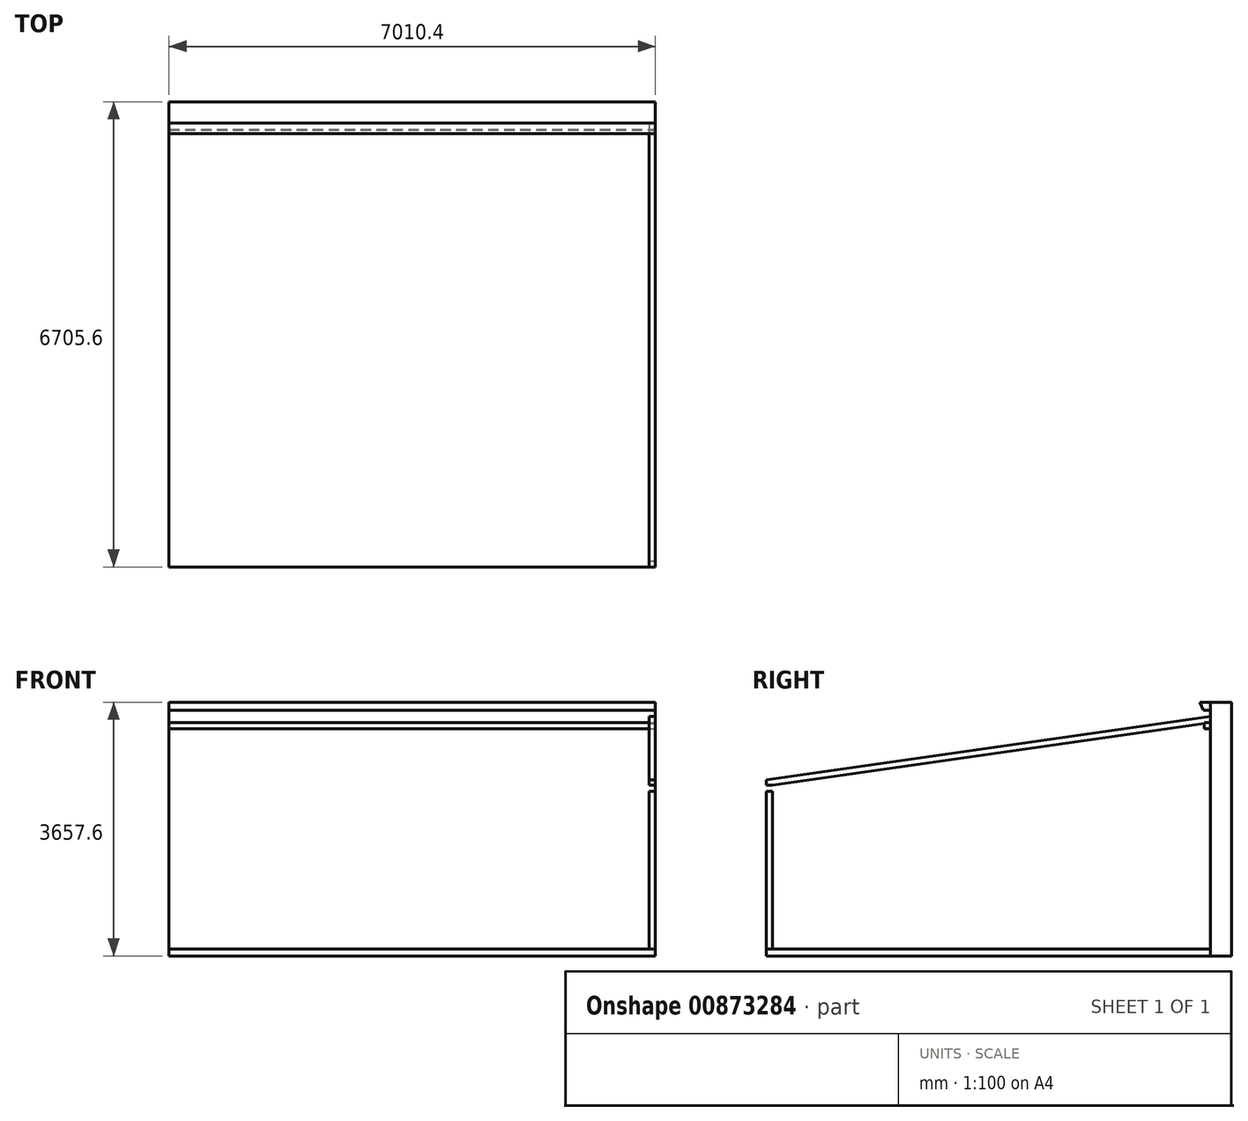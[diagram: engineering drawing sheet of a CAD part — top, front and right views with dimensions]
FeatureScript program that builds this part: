
annotation { "Feature Type Name" : "Feature", "Feature Type Description" : "" }
export const myFeature = defineFeature(function(context is Context, id is Id, definition is map)
    precondition{}
    {
        {
            var Q0;
            Q0=qCreatedBy(makeId("Front.planeOp"),FACE);
            var sketch = newSketch(context, id + "F0", { "sketchPlane" : qUnion([Q0])});
            skLineSegment(sketch, "E0", {"start": v(0, 0) * mm, "end": v(3505.2, 0) * mm});
            skLineSegment(sketch, "E1", {"start": v(0, 0) * mm, "end": v(-3505.2, 0) * mm});
            skLineSegment(sketch, "E2.bottom", {"start": v(-3505.2, 0) * mm, "end": v(3505.2, 0) * mm});
            skLineSegment(sketch, "E2.top", {"start": v(-3505.2, 3657.6) * mm, "end": v(3505.2, 3657.6) * mm});
            skLineSegment(sketch, "E2.left", {"start": v(-3505.2, 0) * mm, "end": v(-3505.2, 3657.6) * mm});
            skLineSegment(sketch, "E2.right", {"start": v(3505.2, 0) * mm, "end": v(3505.2, 3657.6) * mm});
            skSolve(sketch);
        }
        {
            var Q0;
            Q0=sQuery(id+"F0.wireOp",EDGE,"E1");
            var Q1;
            Q1=sQuery(id+"F0.wireOp",EDGE,"E0");
            extrude(context, id + "F1", {"bodyType" : ToolBodyType.SURFACE, "surfaceEntities" : qUnion([Q0, Q1]), "depth" : 6400.8 * mm, "offsetDistance" : 25 * mm});
        }
        {
            var Q0;
            Q0 = qSketchRegion(id + "F0", true);
            extrude(context, id + "F2", {"entities" : qUnion([Q0]), "oppositeDirection" : true, "depth" : 304.8 * mm, "offsetDistance" : 25 * mm});
        }
        {
            var Q0;
            Q0=makeQuery(id+"F2.opExtrude","SWEPT_FACE",FACE,{"disambiguationData":[OSD([sQuery(id+"F0.wireOp",EDGE,"E2.right")])]});
            var sketch = newSketch(context, id + "F3", { "sketchPlane" : qUnion([Q0])});
            skLineSegment(sketch, "E3", {"start": v(0, 3657.6) * mm, "end": v(0, 3543.3) * mm});
            skLineSegment(sketch, "E4", {"start": v(0, 3543.3) * mm, "end": v(-101.6, 3543.3) * mm});
            skLineSegment(sketch, "E5", {"start": v(-101.6, 3543.3) * mm, "end": v(-152.4, 3657.6) * mm});
            skLineSegment(sketch, "E6", {"start": v(-152.4, 3657.6) * mm, "end": v(0, 3657.6) * mm});
            skSolve(sketch);
        }
        {
            var Q0;
            Q0=makeQuery(id+"F3.imprint","IMPRINT",FACE,{"disambiguationData":[TD([[makeQuery(id+"F3.imprint","IMPRINT",EDGE,{"derivedFrom":sQuery(id+"F3.wireOp",EDGE,"E3")}),1.0]])]});
            extrude(context, id + "F4", {"entities" : qUnion([Q0]), "oppositeDirection" : true, "depth" : 7010.4 * mm, "offsetDistance" : 25 * mm});
        }
        {
            var Q0;
            Q0=makeQuery(id+"F1.opExtrude","SWEPT_FACE",FACE,{"disambiguationData":[OSD([sQuery(id+"F0.wireOp",EDGE,"E0"),sQuery(id+"F0.wireOp",EDGE,"E1")])]});
            extrude(context, id + "F5", {"entities" : qUnion([Q0]), "depth" : 101.6 * mm, "offsetDistance" : 25 * mm});
        }
        {
            var Q0;
            Q0=makeQuery(id+"F2.opExtrude","SWEPT_FACE",FACE,{"disambiguationData":[OSD([sQuery(id+"F0.wireOp",EDGE,"E2.right")])]});
            var sketch = newSketch(context, id + "F6", { "sketchPlane" : qUnion([Q0])});
            skLineSegment(sketch, "E7", {"start": v(0, 0) * mm, "end": v(0, 101.6) * mm});
            skLineSegment(sketch, "E8", {"start": v(0, 101.6) * mm, "end": v(0, 3454.4) * mm});
            skLineSegment(sketch, "E9", {"start": v(0, 3454.4) * mm, "end": v(-6400.8, 2540) * mm});
            skLineSegment(sketch, "E10", {"start": v(0, 101.6) * mm, "end": v(-6400.8, 101.6) * mm});
            skLineSegment(sketch, "E11", {"start": v(-6400.8, 101.6) * mm, "end": v(-6400.8, 2540) * mm});
            skLineSegment(sketch, "E12", {"start": v(-6400.8, 2450.2) * mm, "end": v(0, 3364.6) * mm});
            skLineSegment(sketch, "E13", {"start": v(-6311.9, 2462.9) * mm, "end": v(-6311.9, 101.6) * mm});
            skLineSegment(sketch, "E14.bottom", {"start": v(0, 3364.6) * mm, "end": v(-88.9, 3364.6) * mm});
            skLineSegment(sketch, "E14.top", {"start": v(0, 3275.7) * mm, "end": v(-88.9, 3275.7) * mm});
            skLineSegment(sketch, "E14.left", {"start": v(0, 3364.6) * mm, "end": v(0, 3275.7) * mm});
            skLineSegment(sketch, "E14.right", {"start": v(-88.9, 3364.6) * mm, "end": v(-88.9, 3275.7) * mm});
            skSolve(sketch);
        }
        {
            var Q0;
            {var subQ3=sQuery(id+"F6.wireOp",EDGE,"E13");Q0=makeQuery(id+"F6.imprint","IMPRINT",FACE,{"disambiguationData":[TD([[makeQuery(id+"F6.imprint","IMPRINT",EDGE,{"derivedFrom":subQ3}),-1.0]])]});}
            extrude(context, id + "F7", {"entities" : qUnion([Q0]), "oppositeDirection" : true, "depth" : 88.9 * mm, "offsetDistance" : 25 * mm});
        }
        {
            var Q0;
            {var subQ4=sQuery(id+"F6.wireOp",EDGE,"E9");Q0=makeQuery(id+"F6.imprint","IMPRINT",FACE,{"disambiguationData":[TD([[makeQuery(id+"F6.imprint","IMPRINT",EDGE,{"derivedFrom":subQ4}),1.0]])]});}
            extrude(context, id + "F8", {"entities" : qUnion([Q0]), "oppositeDirection" : true, "depth" : 88.9 * mm, "offsetDistance" : 25 * mm});
        }
        {
            var Q0;
            {var subQ4=sQuery(id+"F6.wireOp",EDGE,"E14.top");Q0=makeQuery(id+"F6.imprint","IMPRINT",FACE,{"disambiguationData":[TD([[makeQuery(id+"F6.imprint","IMPRINT",EDGE,{"derivedFrom":subQ4}),-1.0]])]});}
            var Q1;
            {var subQ0=sQuery(id+"F6.wireOp",EDGE,"E14.bottom");Q1=makeQuery(id+"F6.imprint","IMPRINT",FACE,{"disambiguationData":[TD([[makeQuery(id+"F6.imprint","IMPRINT",EDGE,{"derivedFrom":subQ0}),1.0]])]});}
            extrude(context, id + "F9", {"entities" : qUnion([Q0, Q1]), "oppositeDirection" : true, "depth" : 7010.4 * mm, "offsetDistance" : 25 * mm});
        }
        {
            var Q0;
            Q0=makeQuery(id+"F7.opExtrude","CAP_FACE",FACE,{"disambiguationData":[OSD([sQuery(id+"F6.wireOp",EDGE,"E10"),sQuery(id+"F6.wireOp",EDGE,"E11"),sQuery(id+"F6.wireOp",EDGE,"E12"),sQuery(id+"F6.wireOp",EDGE,"E13")])],"isStart":true});
            var sketch = newSketch(context, id + "F10", { "sketchPlane" : qUnion([Q0])});
            skLineSegment(sketch, "E15.bottom", {"start": v(-6311.9, 2462.9) * mm, "end": v(-6400.8, 2462.9) * mm});
            skLineSegment(sketch, "E15.top", {"start": v(-6311.9, 2374) * mm, "end": v(-6400.8, 2374) * mm});
            skLineSegment(sketch, "E15.left", {"start": v(-6311.9, 2462.9) * mm, "end": v(-6311.9, 2374) * mm});
            skLineSegment(sketch, "E15.right", {"start": v(-6400.8, 2462.9) * mm, "end": v(-6400.8, 2374) * mm});
            skSolve(sketch);
        }
        {
            var Q0;
            {var subQ0=sQuery(id+"F10.wireOp",EDGE,"E15.top");Q0=makeQuery(id+"F10.imprint","IMPRINT",FACE,{"disambiguationData":[TD([[makeQuery(id+"F10.imprint","IMPRINT",EDGE,{"derivedFrom":subQ0}),-1.0]])]});}
            var Q1;
            {var subQ0=sQuery(id+"F10.wireOp",EDGE,"E15.bottom");Q1=makeQuery(id+"F10.imprint","IMPRINT",FACE,{"disambiguationData":[TD([[makeQuery(id+"F10.imprint","IMPRINT",EDGE,{"derivedFrom":subQ0}),1.0]])]});}
            extrude(context, id + "F11", {"entities" : qUnion([Q0, Q1]), "operationType" : NewBodyOperationType.REMOVE, "oppositeDirection" : true, "depth" : 88.9 * mm, "offsetDistance" : 25 * mm});
        }
    });
